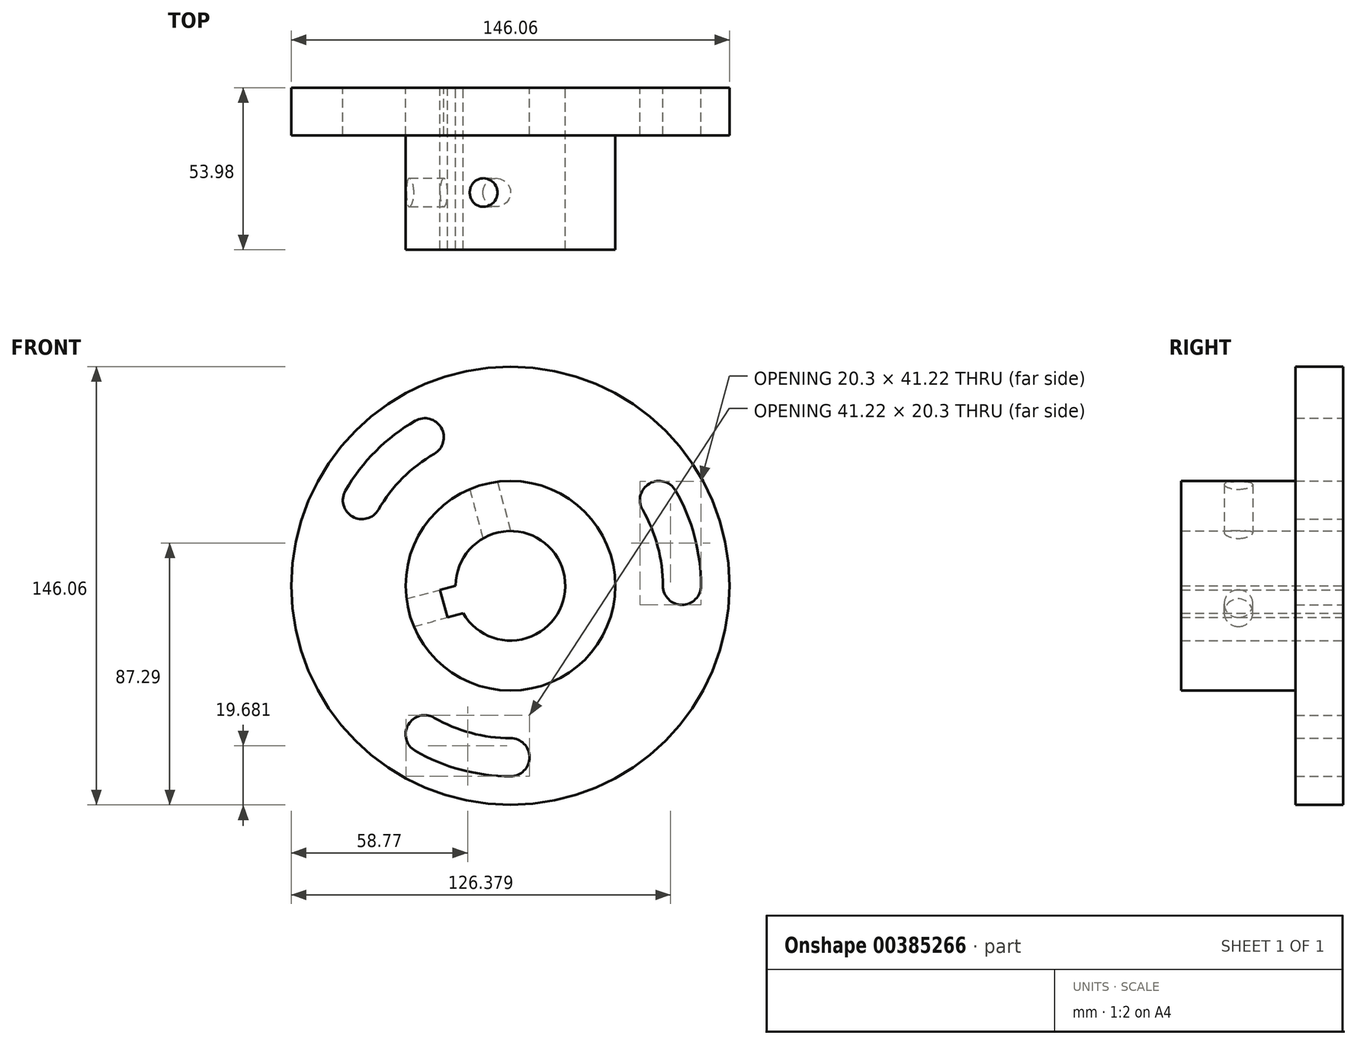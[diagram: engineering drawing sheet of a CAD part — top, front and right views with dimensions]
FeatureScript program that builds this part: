
annotation { "Feature Type Name" : "Feature", "Feature Type Description" : "" }
export const myFeature = defineFeature(function(context is Context, id is Id, definition is map)
    precondition{}
    {
        {
            var Q0;
            Q0=qCreatedBy(makeId("Front.planeOp"),FACE);
            var sketch = newSketch(context, id + "F0", { "sketchPlane" : qUnion([Q0])});
            skCircle(sketch, "E0", {"center": v(0, 0) * mm, "radius": 73.03 * mm});
            skCircle(sketch, "E1", {"center": v(0, 0) * mm, "radius": 18.26 * mm});
            skArc(sketch, "E2", {"start": v(50.8, 0) * mm, "mid": v(49.07, 13.15) * mm, "end": v(44, 25.4) * mm});
            skArc(sketch, "E3", {"start": v(63.5, 0) * mm, "mid": v(61.34, 16.44) * mm, "end": v(55, 31.75) * mm});
            skLineSegment(sketch, "E4", {"start": v(0, 0) * mm, "end": v(18.26, 0) * mm});
            skLineSegment(sketch, "E5.trimOffspring", {"start": v(73.03, 0) * mm, "end": v(85.4, 0) * mm});
            skArc(sketch, "E6", {"start": v(55, 31.75) * mm, "mid": v(46.32, 34.07) * mm, "end": v(44, 25.4) * mm});
            skArc(sketch, "E7", {"start": v(50.8, 0) * mm, "mid": v(57.15, -6.35) * mm, "end": v(63.5, 0) * mm});
            skArc(sketch, "E8.1.1", {"start": v(-25.4, 44) * mm, "mid": v(-23.08, 52.67) * mm, "end": v(-31.75, 55) * mm});
            skArc(sketch, "E8.1.2", {"start": v(-31.75, 55) * mm, "mid": v(-44.9, 44.9) * mm, "end": v(-55, 31.75) * mm});
            skArc(sketch, "E8.1.3", {"start": v(-55, 31.75) * mm, "mid": v(-52.67, 23.08) * mm, "end": v(-44, 25.4) * mm});
            skArc(sketch, "E8.1.4", {"start": v(-25.4, 44) * mm, "mid": v(-35.92, 35.92) * mm, "end": v(-44, 25.4) * mm});
            skArc(sketch, "E8.2.1", {"start": v(-25.4, -44) * mm, "mid": v(-34.07, -46.32) * mm, "end": v(-31.75, -55) * mm});
            skArc(sketch, "E8.2.2", {"start": v(-31.75, -55) * mm, "mid": v(-16.44, -61.34) * mm, "end": v(0, -63.5) * mm});
            skArc(sketch, "E8.2.3", {"start": v(0, -63.5) * mm, "mid": v(6.35, -57.15) * mm, "end": v(0, -50.8) * mm});
            skArc(sketch, "E8.2.4", {"start": v(-25.4, -44) * mm, "mid": v(-13.15, -49.07) * mm, "end": v(0, -50.8) * mm});
            skLineSegment(sketch, "E9", {"start": v(0, 0) * mm, "end": v(49.5, 28.58) * mm});
            skLineSegment(sketch, "E10", {"start": v(0, 0) * mm, "end": v(0, 85.73) * mm});
            skSolve(sketch);
        }
        {
            var Q0;
            Q0 = qSketchRegion(id + "F0", true);
            extrude(context, id + "F1", {"entities" : qUnion([Q0]), "offsetDistance" : 25.4 * mm, "depth" : 15.88 * mm});
        }
        {
            var Q0;
            Q0=makeQuery(id+"F1.opExtrude","CAP_FACE",FACE,{"disambiguationData":[OSD([sQuery(id+"F0.wireOp",EDGE,"E0")])],"isStart":false});
            var sketch = newSketch(context, id + "F2", { "sketchPlane" : qUnion([Q0])});
            skCircle(sketch, "E11", {"center": v(0, 0) * mm, "radius": 34.93 * mm});
            skCircle(sketch, "E12.0", {"center": v(0, 0) * mm, "radius": 18.26 * mm});
            skLineSegment(sketch, "E13", {"start": v(0, 0) * mm, "end": v(-22.87, 0) * mm});
            skPoint(sketch, "E14.middle", {"position": v(-18.26, 0) * mm});
            skSolve(sketch);
        }
        {
            var Q0;
            Q0 = qSketchRegion(id + "F2", true);
            extrude(context, id + "F3", {"entities" : qUnion([Q0]), "operationType" : NewBodyOperationType.ADD, "offsetDistance" : 25.4 * mm, "depth" : 38.1 * mm});
        }
        {
            var Q0;
            Q0=qCreatedBy(makeId("Front.planeOp"),FACE);
            var sketch = newSketch(context, id + "F4", { "sketchPlane" : qUnion([Q0])});
            skCircle(sketch, "E15.0", {"center": v(0, 0) * mm, "radius": 18.26 * mm});
            skLineSegment(sketch, "E16", {"start": v(-70.54, -18.9) * mm, "end": v(49.07, 13.15) * mm});
            skLineSegment(sketch, "E17", {"start": v(-17.63, -4.73) * mm, "end": v(-18.87, -0.12) * mm});
            skLineSegment(sketch, "E18", {"start": v(-23.47, -1.36) * mm, "end": v(-21, -10.56) * mm});
            skLineSegment(sketch, "E19", {"start": v(-21, -10.56) * mm, "end": v(-11.8, -8.1) * mm});
            skLineSegment(sketch, "E20", {"start": v(-17.63, -4.73) * mm, "end": v(-13.03, -3.5) * mm});
            skLineSegment(sketch, "E21", {"start": v(-13.03, -3.5) * mm, "end": v(-14.27, 1.1) * mm});
            skLineSegment(sketch, "E22", {"start": v(-14.27, 1.1) * mm, "end": v(-11.8, -8.1) * mm});
            skLineSegment(sketch, "E23", {"start": v(-23.47, -1.36) * mm, "end": v(-14.27, 1.1) * mm});
            skSolve(sketch);
        }
        {
            var Q0;
            Q0 = qSketchRegion(id + "F4", true);
            var Q1;
            Q1=makeQuery(id+"F3.opExtrude","CAP_FACE",FACE,{"disambiguationData":[OSD([sQuery(id+"F2.wireOp",EDGE,"E11"),sQuery(id+"F2.wireOp",EDGE,"E12.0")])],"isStart":false});
            var Q2;
            {var subQ5=sQuery(id+"F4.wireOp",EDGE,"E21");Q2=makeQuery(id+"F4.imprint","IMPRINT",FACE,{"disambiguationData":[TD([[makeQuery(id+"F4.imprint","IMPRINT",EDGE,{"derivedFrom":subQ5}),1.0]])]});}
            var Q3;
            {var subQ5=sQuery(id+"F4.wireOp",EDGE,"E22");Q3=makeQuery(id+"F4.imprint","IMPRINT",FACE,{"disambiguationData":[TD([[makeQuery(id+"F4.imprint","IMPRINT",EDGE,{"derivedFrom":subQ5}),-1.0]])]});}
            extrude(context, id + "F5", {"entities" : qUnion([Q0, Q1, Q2, Q3]), "operationType" : NewBodyOperationType.REMOVE, "depth" : 76.2 * mm, "offsetDistance" : 25.4 * mm});
        }
        {
            var Q0;
            Q0=makeQuery(id+"F5.boolean.opBoolean","COPY",FACE,{"derivedFrom":makeQuery(id+"F5.opExtrude","SWEPT_FACE",FACE,{"disambiguationData":[OSD([sQuery(id+"F4.wireOp",EDGE,"E18")])]})});
            var sketch = newSketch(context, id + "F6", { "sketchPlane" : qUnion([Q0])});
            skCircle(sketch, "E24", {"center": v(-34.92, 0) * mm, "radius": 4.76 * mm});
            skSolve(sketch);
        }
        {
            var Q0;
            Q0 = qSketchRegion(id + "F6", true);
            extrude(context, id + "F7", {"entities" : qUnion([Q0]), "operationType" : NewBodyOperationType.REMOVE, "oppositeDirection" : true, "depth" : 25.4 * mm, "offsetDistance" : 25.4 * mm});
        }
        {
            var Q0;
            Q0=makeQuery(id+"F5.boolean.opBoolean","COPY",FACE,{"derivedFrom":makeQuery(id+"F5.opExtrude","SWEPT_FACE",FACE,{"disambiguationData":[OSD([sQuery(id+"F4.wireOp",EDGE,"E23")])]})});
            var sketch = newSketch(context, id + "F8", { "sketchPlane" : qUnion([Q0])});
            skCircle(sketch, "E25", {"center": v(0, 34.92) * mm, "radius": 4.76 * mm});
            skSolve(sketch);
        }
        {
            var Q0;
            Q0 = qSketchRegion(id + "F8", true);
            extrude(context, id + "F9", {"entities" : qUnion([Q0]), "operationType" : NewBodyOperationType.REMOVE, "oppositeDirection" : true, "depth" : 50.8 * mm, "offsetDistance" : 25.4 * mm});
        }
    });
